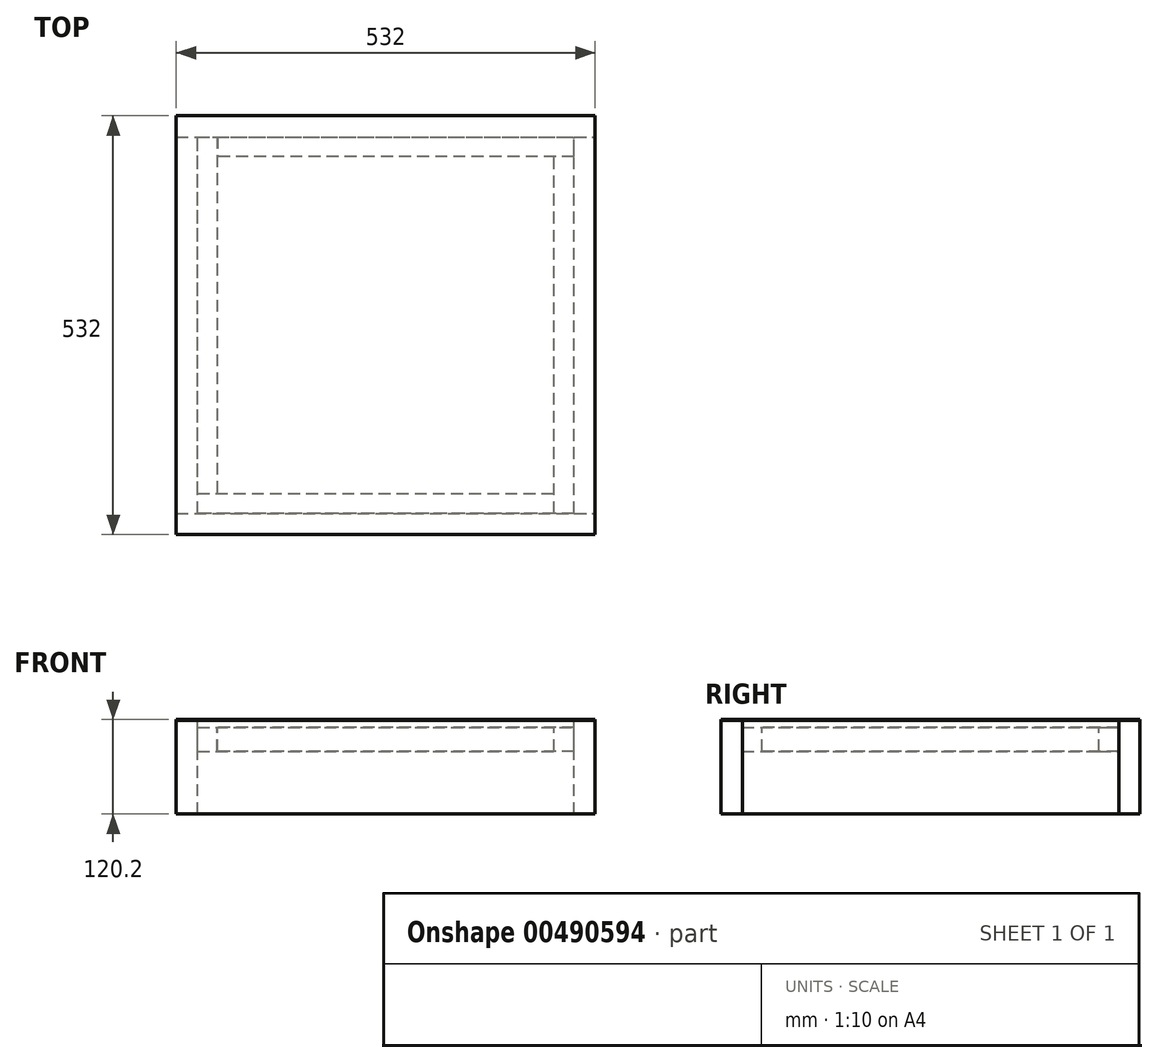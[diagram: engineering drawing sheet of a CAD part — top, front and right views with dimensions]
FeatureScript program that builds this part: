
annotation { "Feature Type Name" : "Feature", "Feature Type Description" : "" }
export const myFeature = defineFeature(function(context is Context, id is Id, definition is map)
    precondition{}
    {
        {
            var Q0;
            Q0=qCreatedBy(makeId("Front.planeOp"),FACE);
            var sketch = newSketch(context, id + "F0", { "sketchPlane" : qUnion([Q0])});
            skLineSegment(sketch, "E0", {"start": v(-239, 0) * mm, "end": v(-239, 119) * mm});
            skLineSegment(sketch, "E1", {"start": v(-239, 119) * mm, "end": v(-266, 119) * mm});
            skLineSegment(sketch, "E2", {"start": v(-266, 119) * mm, "end": v(-266, 0) * mm});
            skLineSegment(sketch, "E3", {"start": v(-266, 0) * mm, "end": v(-239, 0) * mm});
            skPoint(sketch, "E4.start.orphan", {"position": v(0, 0) * mm});
            skLineSegment(sketch, "E5", {"start": v(0, 0) * mm, "end": v(0, -109.79) * mm, "construction": true});
            skLineSegment(sketch, "E6.MirrorCS", {"start": v(266, 0) * mm, "end": v(239, 0) * mm});
            skLineSegment(sketch, "E7.MirrorCS", {"start": v(239, 119) * mm, "end": v(266, 119) * mm});
            skLineSegment(sketch, "E8.MirrorCS", {"start": v(266, 119) * mm, "end": v(266, 0) * mm});
            skLineSegment(sketch, "E9.MirrorCS", {"start": v(239, 0) * mm, "end": v(239, 119) * mm});
            skSolve(sketch);
        }
        {
            var Q0;
            Q0 = qSketchRegion(id + "F0", true);
            extrude(context, id + "F1", {"entities" : qUnion([Q0]), "offsetDistance" : 25 * mm, "depth" : 478 * mm, "symmetric" : true});
        }
        {
            var Q0;
            Q0=makeQuery(id+"F1.opExtrude","CAP_FACE",FACE,{"disambiguationData":[OSD([sQuery(id+"F0.wireOp",EDGE,"E0"),sQuery(id+"F0.wireOp",EDGE,"E1"),sQuery(id+"F0.wireOp",EDGE,"E2"),sQuery(id+"F0.wireOp",EDGE,"E3")])],"isStart":false});
            var sketch = newSketch(context, id + "F2", { "sketchPlane" : qUnion([Q0])});
            skLineSegment(sketch, "E10", {"start": v(0, 0) * mm, "end": v(0, 80.7) * mm, "construction": true});
            skLineSegment(sketch, "E11.0", {"start": v(-266, 119) * mm, "end": v(266, 119) * mm});
            skLineSegment(sketch, "E12.0", {"start": v(-266, 0) * mm, "end": v(266, 0) * mm});
            skLineSegment(sketch, "E13.0", {"start": v(-266, 119) * mm, "end": v(-266, 0) * mm});
            skLineSegment(sketch, "E14.0", {"start": v(266, 119) * mm, "end": v(266, 0) * mm});
            skSolve(sketch);
        }
        {
            var Q0;
            Q0 = qSketchRegion(id + "F2", true);
            extrude(context, id + "F3", {"entities" : qUnion([Q0]), "offsetDistance" : 25 * mm, "depth" : 27 * mm});
        }
        {
            var Q0;
            Q0=makeQuery(id+"F3.opExtrude","SWEPT_BODY",BODY,{"disambiguationData":[OSD([sQuery(id+"F2.wireOp",EDGE,"E11.0"),sQuery(id+"F2.wireOp",EDGE,"E12.0"),sQuery(id+"F2.wireOp",EDGE,"E12.1"),sQuery(id+"F2.wireOp",EDGE,"E12.2"),sQuery(id+"F2.wireOp",EDGE,"E12.3"),sQuery(id+"F2.wireOp",EDGE,"E12.4"),sQuery(id+"F2.wireOp",EDGE,"E12.5"),sQuery(id+"F2.wireOp",EDGE,"E12.6"),sQuery(id+"F2.wireOp",EDGE,"E12.7"),sQuery(id+"F2.wireOp",EDGE,"E12.8"),sQuery(id+"F2.wireOp",EDGE,"E12.9"),sQuery(id+"F2.wireOp",EDGE,"E12.10"),sQuery(id+"F2.wireOp",EDGE,"E12.11"),sQuery(id+"F2.wireOp",EDGE,"a57a3b10-a078-487a-a44a-061c31cd21020.MirrorCS"),sQuery(id+"F2.wireOp",EDGE,"a57a3b10-a078-487a-a44a-061c31cd21021.MirrorCS"),sQuery(id+"F2.wireOp",EDGE,"a57a3b10-a078-487a-a44a-061c31cd21022.MirrorCS"),sQuery(id+"F2.wireOp",EDGE,"a57a3b10-a078-487a-a44a-061c31cd21023.MirrorCS"),sQuery(id+"F2.wireOp",EDGE,"a57a3b10-a078-487a-a44a-061c31cd21024.MirrorCS"),sQuery(id+"F2.wireOp",EDGE,"a57a3b10-a078-487a-a44a-061c31cd21028.MirrorCS"),sQuery(id+"F2.wireOp",EDGE,"a57a3b10-a078-487a-a44a-061c31cd21029.MirrorCS"),sQuery(id+"F2.wireOp",EDGE,"a57a3b10-a078-487a-a44a-061c31cd210210.MirrorCS"),sQuery(id+"F2.wireOp",EDGE,"a57a3b10-a078-487a-a44a-061c31cd210211.MirrorCS"),sQuery(id+"F2.wireOp",EDGE,"a57a3b10-a078-487a-a44a-061c31cd210212.MirrorCS"),sQuery(id+"F2.wireOp",EDGE,"a57a3b10-a078-487a-a44a-061c31cd210213.MirrorCS")])]});
            var Q1;
            Q1=qCreatedBy(makeId("Front.planeOp"),FACE);
            mirror(context, id + "F4", {"entities" : qUnion([Q0]), "mirrorPlane" : qUnion([Q1])});
        }
        {
            var Q0;
            Q0=makeQuery(id+"F1.opExtrude","SWEPT_FACE",FACE,{"disambiguationData":[OSD([sQuery(id+"F0.wireOp",EDGE,"E7.MirrorCS")])]});
            var sketch = newSketch(context, id + "F5", { "sketchPlane" : qUnion([Q0])});
            skLineSegment(sketch, "E15.0", {"start": v(-239, -239) * mm, "end": v(-239, 239) * mm});
            skLineSegment(sketch, "E15.1", {"start": v(239, -239) * mm, "end": v(239, 239) * mm});
            skLineSegment(sketch, "E16", {"start": v(-239, 239) * mm, "end": v(239, 239) * mm});
            skLineSegment(sketch, "E17", {"start": v(239, -239) * mm, "end": v(-239, -239) * mm});
            skSolve(sketch);
        }
        {
            var Q0;
            Q0 = qSketchRegion(id + "F5", true);
            extrude(context, id + "F6", {"entities" : qUnion([Q0]), "oppositeDirection" : true, "offsetDistance" : 25 * mm, "depth" : 9 * mm});
        }
        {
            var Q0;
            Q0=makeQuery(id+"F6.opExtrude","CAP_FACE",FACE,{"disambiguationData":[OSD([sQuery(id+"F5.wireOp",EDGE,"E15.0"),sQuery(id+"F5.wireOp",EDGE,"E15.1"),sQuery(id+"F5.wireOp",EDGE,"E16"),sQuery(id+"F5.wireOp",EDGE,"E17")])],"isStart":false});
            var sketch = newSketch(context, id + "F7", { "sketchPlane" : qUnion([Q0])});
            skLineSegment(sketch, "E18.0", {"start": v(-239, 213.9) * mm, "end": v(-239, -239) * mm});
            skLineSegment(sketch, "E19", {"start": v(-239, -239) * mm, "end": v(-214, -239) * mm});
            skLineSegment(sketch, "E20", {"start": v(-214, -239) * mm, "end": v(-214, 213.9) * mm});
            skLineSegment(sketch, "E21.0", {"start": v(-239, 213.9) * mm, "end": v(-214, 213.9) * mm});
            skPoint(sketch, "E22.center", {"position": v(12, 0) * mm});
            skLineSegment(sketch, "E23.1.0", {"start": v(-213.9, -239) * mm, "end": v(239, -239) * mm});
            skLineSegment(sketch, "E23.1.1", {"start": v(239, -214) * mm, "end": v(-213.9, -214) * mm});
            skLineSegment(sketch, "E23.1.2", {"start": v(239, -239) * mm, "end": v(239, -214) * mm});
            skLineSegment(sketch, "E23.1.3", {"start": v(-213.9, -239) * mm, "end": v(-213.9, -214) * mm});
            skLineSegment(sketch, "E23.2.0", {"start": v(239, -213.9) * mm, "end": v(239, 239) * mm});
            skLineSegment(sketch, "E23.2.1", {"start": v(214, 239) * mm, "end": v(214, -213.9) * mm});
            skLineSegment(sketch, "E23.2.2", {"start": v(239, 239) * mm, "end": v(214, 239) * mm});
            skLineSegment(sketch, "E23.2.3", {"start": v(239, -213.9) * mm, "end": v(214, -213.9) * mm});
            skLineSegment(sketch, "E23.3.0", {"start": v(213.9, 239) * mm, "end": v(-239, 239) * mm});
            skLineSegment(sketch, "E23.3.1", {"start": v(-239, 214) * mm, "end": v(213.9, 214) * mm});
            skLineSegment(sketch, "E23.3.2", {"start": v(-239, 239) * mm, "end": v(-239, 214) * mm});
            skLineSegment(sketch, "E23.3.3", {"start": v(213.9, 239) * mm, "end": v(213.9, 214) * mm});
            skPoint(sketch, "E23.center", {"position": v(0, 0) * mm});
            skSolve(sketch);
        }
        {
            var Q0;
            Q0 = qSketchRegion(id + "F7", true);
            extrude(context, id + "F8", {"entities" : qUnion([Q0]), "depth" : 30 * mm, "offsetDistance" : 25 * mm});
        }
        {
            var Q0;
            Q0=makeQuery(id+"F6.opExtrude","CAP_FACE",FACE,{"disambiguationData":[OSD([sQuery(id+"F5.wireOp",EDGE,"E15.0"),sQuery(id+"F5.wireOp",EDGE,"E15.1"),sQuery(id+"F5.wireOp",EDGE,"E16"),sQuery(id+"F5.wireOp",EDGE,"E17")])],"isStart":true});
            var sketch = newSketch(context, id + "F9", { "sketchPlane" : qUnion([Q0])});
            skLineSegment(sketch, "E24.0", {"start": v(-266, 266) * mm, "end": v(266, 266) * mm});
            skLineSegment(sketch, "E24.1", {"start": v(-266, -266) * mm, "end": v(266, -266) * mm});
            skLineSegment(sketch, "E25", {"start": v(-266, 266) * mm, "end": v(-266, -266) * mm});
            skLineSegment(sketch, "E26", {"start": v(266, 266) * mm, "end": v(266, -266) * mm});
            skSolve(sketch);
        }
        {
            var Q0;
            Q0 = qSketchRegion(id + "F9", true);
            extrude(context, id + "F10", {"entities" : qUnion([Q0]), "depth" : 1.2 * mm, "offsetDistance" : 25 * mm});
        }
    });
